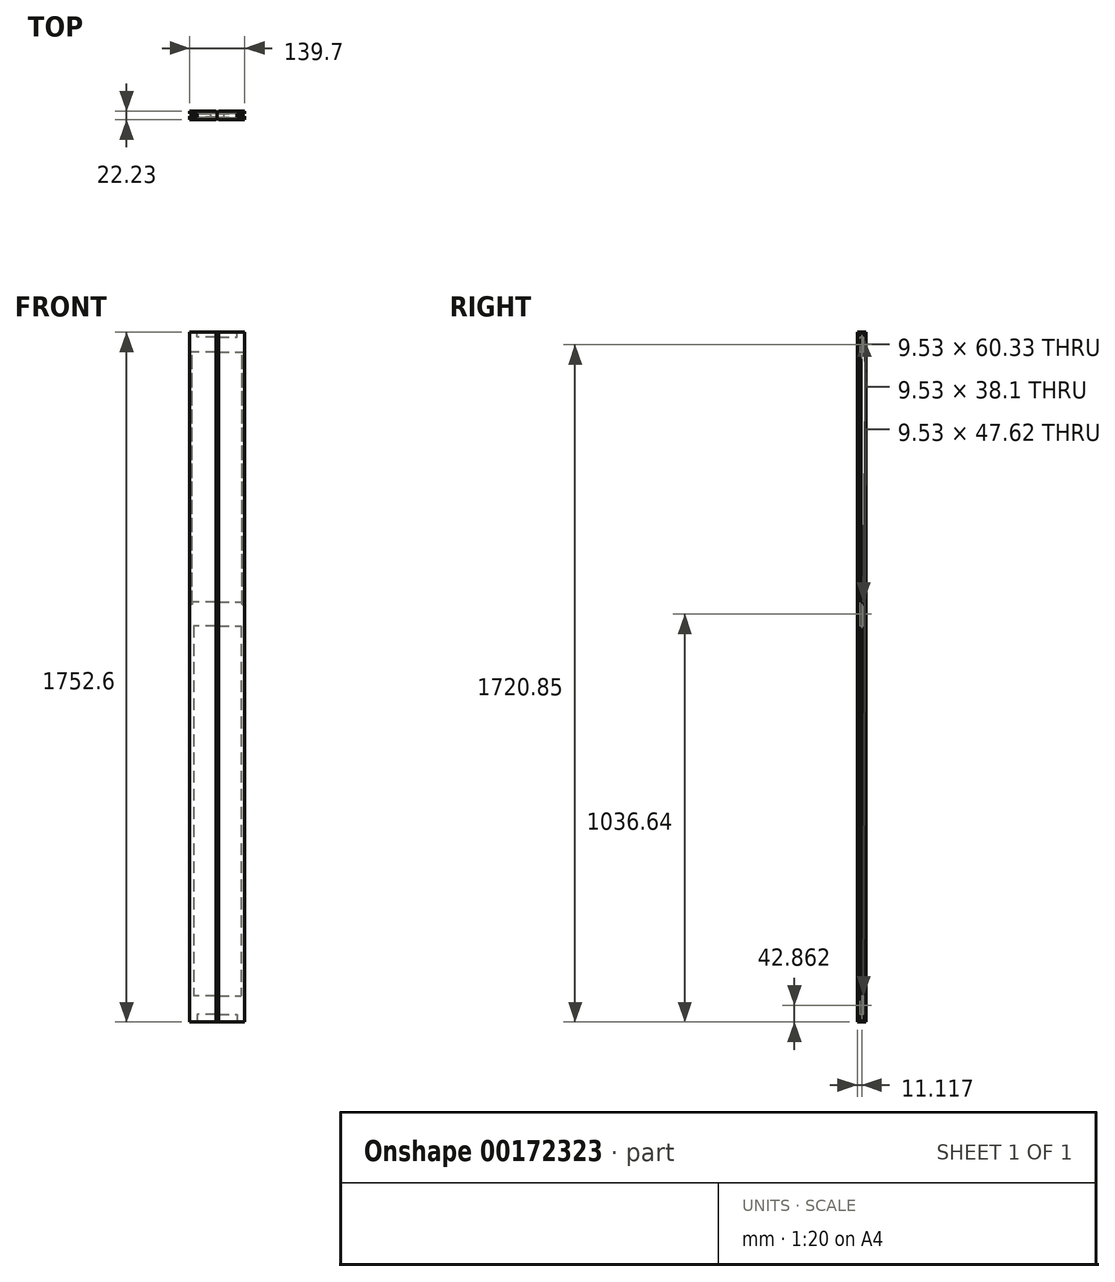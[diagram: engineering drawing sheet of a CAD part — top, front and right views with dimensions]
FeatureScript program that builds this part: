
annotation { "Feature Type Name" : "Feature", "Feature Type Description" : "" }
export const myFeature = defineFeature(function(context is Context, id is Id, definition is map)
    precondition{}
    {
        {
            var Q0;
            Q0=qCreatedBy(makeId("Front.planeOp"),FACE);
            var sketch = newSketch(context, id + "F0", { "sketchPlane" : qUnion([Q0])});
            skLineSegment(sketch, "E0.bottom", {"start": v(0, 0) * mm, "end": v(69.85, 0) * mm});
            skLineSegment(sketch, "E0.top", {"start": v(0, 1778) * mm, "end": v(69.85, 1778) * mm});
            skLineSegment(sketch, "E0.left", {"start": v(0, 0) * mm, "end": v(0, 1778) * mm});
            skLineSegment(sketch, "E0.right", {"start": v(69.85, 0) * mm, "end": v(69.85, 1778) * mm});
            skSolve(sketch);
        }
        {
            var Q0;
            Q0=makeQuery(id+"F0.imprint","IMPRINT",FACE,{"disambiguationData":[TD([[makeQuery(id+"F0.imprint","IMPRINT",EDGE,{"derivedFrom":sQuery(id+"F0.wireOp",EDGE,"E0.bottom")}),1.0]])]});
            extrude(context, id + "F1", {"entities" : qUnion([Q0]), "depth" : 22.22 * mm});
        }
        {
            var Q0;
            Q0=makeQuery(id+"F1.opExtrude","SWEPT_FACE",FACE,{"disambiguationData":[OSD([sQuery(id+"F0.wireOp",EDGE,"E0.right")])]});
            var sketch = newSketch(context, id + "F2", { "sketchPlane" : qUnion([Q0])});
            skLineSegment(sketch, "E1.bottom", {"start": v(-15.87, 79.37) * mm, "end": v(-6.35, 79.37) * mm});
            skLineSegment(sketch, "E1.top", {"start": v(-15.87, 0) * mm, "end": v(-6.35, 0) * mm});
            skLineSegment(sketch, "E1.left", {"start": v(-15.88, 79.37) * mm, "end": v(-15.87, 0) * mm});
            skLineSegment(sketch, "E1.right", {"start": v(-6.35, 79.37) * mm, "end": v(-6.35, 0) * mm});
            skLineSegment(sketch, "E2.bottom", {"start": v(-22.23, 88.9) * mm, "end": v(0, 88.9) * mm, "construction": true});
            skLineSegment(sketch, "E2.top", {"start": v(-22.23, 0) * mm, "end": v(0, 0) * mm, "construction": true});
            skLineSegment(sketch, "E2.left", {"start": v(-22.23, 88.9) * mm, "end": v(-22.23, 0) * mm, "construction": true});
            skLineSegment(sketch, "E2.right", {"start": v(0, 88.9) * mm, "end": v(0, 0) * mm, "construction": true});
            skLineSegment(sketch, "E3", {"start": v(-15.88, 31.75) * mm, "end": v(-6.35, 31.75) * mm});
            skLineSegment(sketch, "E4.bottom", {"start": v(-15.88, 1714.5) * mm, "end": v(-6.35, 1714.5) * mm});
            skLineSegment(sketch, "E4.top", {"start": v(-15.88, 1778) * mm, "end": v(-6.35, 1778) * mm});
            skLineSegment(sketch, "E4.left", {"start": v(-15.88, 1714.5) * mm, "end": v(-15.88, 1778) * mm});
            skLineSegment(sketch, "E4.right", {"start": v(-6.35, 1714.5) * mm, "end": v(-6.35, 1778) * mm});
            skLineSegment(sketch, "E5.bottom", {"start": v(0, 1778) * mm, "end": v(-22.23, 1778) * mm, "construction": true});
            skLineSegment(sketch, "E5.top", {"start": v(0, 1689.1) * mm, "end": v(-22.23, 1689.1) * mm, "construction": true});
            skLineSegment(sketch, "E5.left", {"start": v(0, 1778) * mm, "end": v(0, 1689.1) * mm, "construction": true});
            skLineSegment(sketch, "E5.right", {"start": v(-22.23, 1778) * mm, "end": v(-22.23, 1689.1) * mm, "construction": true});
            skLineSegment(sketch, "E6", {"start": v(-15.88, 1752.6) * mm, "end": v(-6.35, 1752.6) * mm});
            skLineSegment(sketch, "E7.bottom", {"start": v(-6.35, 1079.5) * mm, "end": v(-15.88, 1079.5) * mm});
            skLineSegment(sketch, "E7.top", {"start": v(-6.35, 1019.18) * mm, "end": v(-15.88, 1019.18) * mm});
            skLineSegment(sketch, "E7.left", {"start": v(-6.35, 1079.5) * mm, "end": v(-6.35, 1019.18) * mm});
            skLineSegment(sketch, "E7.right", {"start": v(-15.88, 1079.5) * mm, "end": v(-15.88, 1019.18) * mm});
            skLineSegment(sketch, "E8.bottom", {"start": v(-22.23, 1104.9) * mm, "end": v(0, 1104.9) * mm, "construction": true});
            skLineSegment(sketch, "E8.top", {"start": v(-22.23, 993.78) * mm, "end": v(0, 993.78) * mm, "construction": true});
            skLineSegment(sketch, "E8.left", {"start": v(-22.23, 1104.9) * mm, "end": v(-22.23, 993.78) * mm, "construction": true});
            skLineSegment(sketch, "E8.right", {"start": v(0, 1104.9) * mm, "end": v(0, 993.78) * mm, "construction": true});
            skSolve(sketch);
        }
        {
            var Q0;
            {var subQ0=sQuery(id+"F2.wireOp",EDGE,"E1.bottom");Q0=makeQuery(id+"F2.imprint","IMPRINT",FACE,{"disambiguationData":[TD([[makeQuery(id+"F2.imprint","IMPRINT",EDGE,{"derivedFrom":subQ0}),-1.0]])]});}
            var Q1;
            {var subQ0=sQuery(id+"F2.wireOp",EDGE,"E4.bottom");Q1=makeQuery(id+"F2.imprint","IMPRINT",FACE,{"disambiguationData":[TD([[makeQuery(id+"F2.imprint","IMPRINT",EDGE,{"derivedFrom":subQ0}),1.0]])]});}
            var Q2;
            Q2=makeQuery(id+"F2.imprint","IMPRINT",FACE,{"disambiguationData":[TD([[makeQuery(id+"F2.imprint","IMPRINT",EDGE,{"derivedFrom":sQuery(id+"F2.wireOp",EDGE,"E7.bottom")}),1.0]])]});
            extrude(context, id + "F3", {"entities" : qUnion([Q0, Q1, Q2]), "operationType" : NewBodyOperationType.REMOVE, "endBound" : BoundingType.UP_TO_NEXT, "oppositeDirection" : true, "depth" : 25.4 * mm});
        }
        {
            var Q0;
            {var subQ0=sQuery(id+"F2.wireOp",EDGE,"E1.top");Q0=makeQuery(id+"F2.imprint","IMPRINT",FACE,{"disambiguationData":[TD([[makeQuery(id+"F2.imprint","IMPRINT",EDGE,{"derivedFrom":subQ0}),1.0]])]});}
            var Q1;
            {var subQ0=sQuery(id+"F2.wireOp",EDGE,"E4.top");Q1=makeQuery(id+"F2.imprint","IMPRINT",FACE,{"disambiguationData":[TD([[makeQuery(id+"F2.imprint","IMPRINT",EDGE,{"derivedFrom":subQ0}),-1.0]])]});}
            extrude(context, id + "F4", {"entities" : qUnion([Q0, Q1]), "operationType" : NewBodyOperationType.REMOVE, "oppositeDirection" : true, "depth" : 19.05 * mm});
        }
        {
            var Q0;
            Q0=makeQuery(id+"F1.opExtrude","CAP_FACE",FACE,{"disambiguationData":[OSD([sQuery(id+"F0.wireOp",EDGE,"E0.bottom"),sQuery(id+"F0.wireOp",EDGE,"E0.top"),sQuery(id+"F0.wireOp",EDGE,"E0.left"),sQuery(id+"F0.wireOp",EDGE,"E0.right")])],"isStart":false});
            var sketch = newSketch(context, id + "F5", { "sketchPlane" : qUnion([Q0])});
            skLineSegment(sketch, "E9", {"start": v(0, 1765.3) * mm, "end": v(69.85, 1765.3) * mm});
            skLineSegment(sketch, "E10", {"start": v(0, 12.7) * mm, "end": v(69.85, 12.7) * mm});
            skSolve(sketch);
        }
        {
            var Q0;
            {var subQ0=sQuery(id+"F5.wireOp",EDGE,"E10");Q0=makeQuery(id+"F5.imprint","IMPRINT",FACE,{"disambiguationData":[TD([[makeQuery(id+"F5.imprint","IMPRINT",EDGE,{"derivedFrom":subQ0}),-1.0]])]});}
            var Q1;
            {var subQ0=sQuery(id+"F5.wireOp",EDGE,"E9");Q1=makeQuery(id+"F5.imprint","IMPRINT",FACE,{"disambiguationData":[TD([[makeQuery(id+"F5.imprint","IMPRINT",EDGE,{"derivedFrom":subQ0}),1.0]])]});}
            extrude(context, id + "F6", {"entities" : qUnion([Q0, Q1]), "operationType" : NewBodyOperationType.REMOVE, "endBound" : BoundingType.THROUGH_ALL, "oppositeDirection" : true, "depth" : 25.4 * mm});
        }
        {
            var Q0;
            Q0=makeQuery(id+"F1.opExtrude","SWEPT_FACE",FACE,{"disambiguationData":[OSD([sQuery(id+"F0.wireOp",EDGE,"E0.right")])]});
            var sketch = newSketch(context, id + "F7", { "sketchPlane" : qUnion([Q0])});
            skLineSegment(sketch, "E11.bottom", {"start": v(-15.88, 79.37) * mm, "end": v(-6.35, 79.37) * mm});
            skLineSegment(sketch, "E11.top", {"start": v(-15.88, 1019.18) * mm, "end": v(-6.35, 1019.18) * mm});
            skLineSegment(sketch, "E11.left", {"start": v(-15.88, 79.37) * mm, "end": v(-15.88, 1019.18) * mm});
            skLineSegment(sketch, "E11.right", {"start": v(-6.35, 79.37) * mm, "end": v(-6.35, 1019.18) * mm});
            skLineSegment(sketch, "E12.bottom", {"start": v(0, 1073.15) * mm, "end": v(-12.7, 1073.15) * mm});
            skLineSegment(sketch, "E12.top", {"start": v(0, 1714.5) * mm, "end": v(-12.7, 1714.5) * mm});
            skLineSegment(sketch, "E12.left", {"start": v(0, 1073.15) * mm, "end": v(0, 1714.5) * mm});
            skLineSegment(sketch, "E12.right", {"start": v(-12.7, 1073.15) * mm, "end": v(-12.7, 1714.5) * mm});
            skSolve(sketch);
        }
        {
            var Q0;
            {var subQ0=sQuery(id+"F7.wireOp",EDGE,"E11.top");Q0=makeQuery(id+"F7.imprint","IMPRINT",FACE,{"disambiguationData":[TD([[makeQuery(id+"F7.imprint","IMPRINT",EDGE,{"derivedFrom":subQ0}),-1.0]])]});}
            var Q1;
            {var subQ0=sQuery(id+"F7.wireOp",EDGE,"E11.bottom");Q1=makeQuery(id+"F7.imprint","IMPRINT",FACE,{"disambiguationData":[TD([[makeQuery(id+"F7.imprint","IMPRINT",EDGE,{"derivedFrom":subQ0}),1.0]])]});}
            extrude(context, id + "F8", {"entities" : qUnion([Q0, Q1]), "operationType" : NewBodyOperationType.REMOVE, "oppositeDirection" : true, "depth" : 9.52 * mm});
        }
        {
            var Q0;
            Q0=makeQuery(id+"F6.boolean.opBoolean","COPY",FACE,{"derivedFrom":makeQuery(id+"F6.opExtrude","SWEPT_FACE",FACE,{"disambiguationData":[OSD([sQuery(id+"F5.wireOp",EDGE,"E10")])]})});
            var sketch = newSketch(context, id + "F9", { "sketchPlane" : qUnion([Q0])});
            skArc(sketch, "E13", {"start": v(20.64, 16.67) * mm, "mid": v(15.88, 11.9) * mm, "end": v(20.64, 7.14) * mm});
            skArc(sketch, "E14", {"start": v(61.91, 7.14) * mm, "mid": v(66.67, 11.9) * mm, "end": v(61.91, 16.67) * mm});
            skLineSegment(sketch, "E15", {"start": v(20.64, 16.67) * mm, "end": v(61.91, 16.67) * mm});
            skLineSegment(sketch, "E16", {"start": v(61.91, 7.14) * mm, "end": v(20.64, 7.14) * mm});
            skLineSegment(sketch, "E17", {"start": v(20.64, 11.9) * mm, "end": v(61.91, 11.9) * mm, "construction": true});
            skSolve(sketch);
        }
        {
            var Q0;
            Q0=makeQuery(id+"F1.opExtrude","CAP_EDGE",EDGE,{"disambiguationData":[OSD([sQuery(id+"F0.wireOp",EDGE,"E0.left")])],"isStart":false});
            var Q1;
            Q1=makeQuery(id+"F1.opExtrude","CAP_EDGE",EDGE,{"disambiguationData":[OSD([sQuery(id+"F0.wireOp",EDGE,"E0.left")])],"isStart":true});
            chamfer(context, id + "F10", {"entities" : qUnion([Q0, Q1]), "width" : 3.17 * mm, "tangentPropagation" : true});
        }
        {
            var Q0;
            {var subQ5=sQuery(id+"F9.wireOp",EDGE,"E15");Q0=makeQuery(id+"F9.imprint","IMPRINT",FACE,{"disambiguationData":[TD([[makeQuery(id+"F9.imprint","IMPRINT",EDGE,{"derivedFrom":subQ5}),-1.0]])]});}
            extrude(context, id + "F11", {"entities" : qUnion([Q0]), "operationType" : NewBodyOperationType.REMOVE, "oppositeDirection" : true, "depth" : 1.98 * mm});
        }
        {
            var Q0;
            {var subQ3=sQuery(id+"F7.wireOp",EDGE,"E12.left");Q0=makeQuery(id+"F7.imprint","IMPRINT",FACE,{"disambiguationData":[TD([[makeQuery(id+"F7.imprint","IMPRINT",EDGE,{"derivedFrom":subQ3}),1.0]])]});}
            extrude(context, id + "F12", {"entities" : qUnion([Q0]), "operationType" : NewBodyOperationType.REMOVE, "oppositeDirection" : true, "depth" : 6.35 * mm});
        }
        {
            var Q0;
            Q0=makeQuery(id+"F1.opExtrude","SWEPT_BODY",BODY,{"disambiguationData":[OSD([sQuery(id+"F0.wireOp",EDGE,"E0.bottom"),sQuery(id+"F0.wireOp",EDGE,"E0.top"),sQuery(id+"F0.wireOp",EDGE,"E0.left"),sQuery(id+"F0.wireOp",EDGE,"E0.right")])]});
            var Q1;
            Q1=makeQuery(id+"F1.opExtrude","SWEPT_FACE",FACE,{"disambiguationData":[OSD([sQuery(id+"F0.wireOp",EDGE,"E0.left")])]});
            mirror(context, id + "F13", {"entities" : qUnion([Q0]), "mirrorPlane" : qUnion([Q1])});
        }
    });
